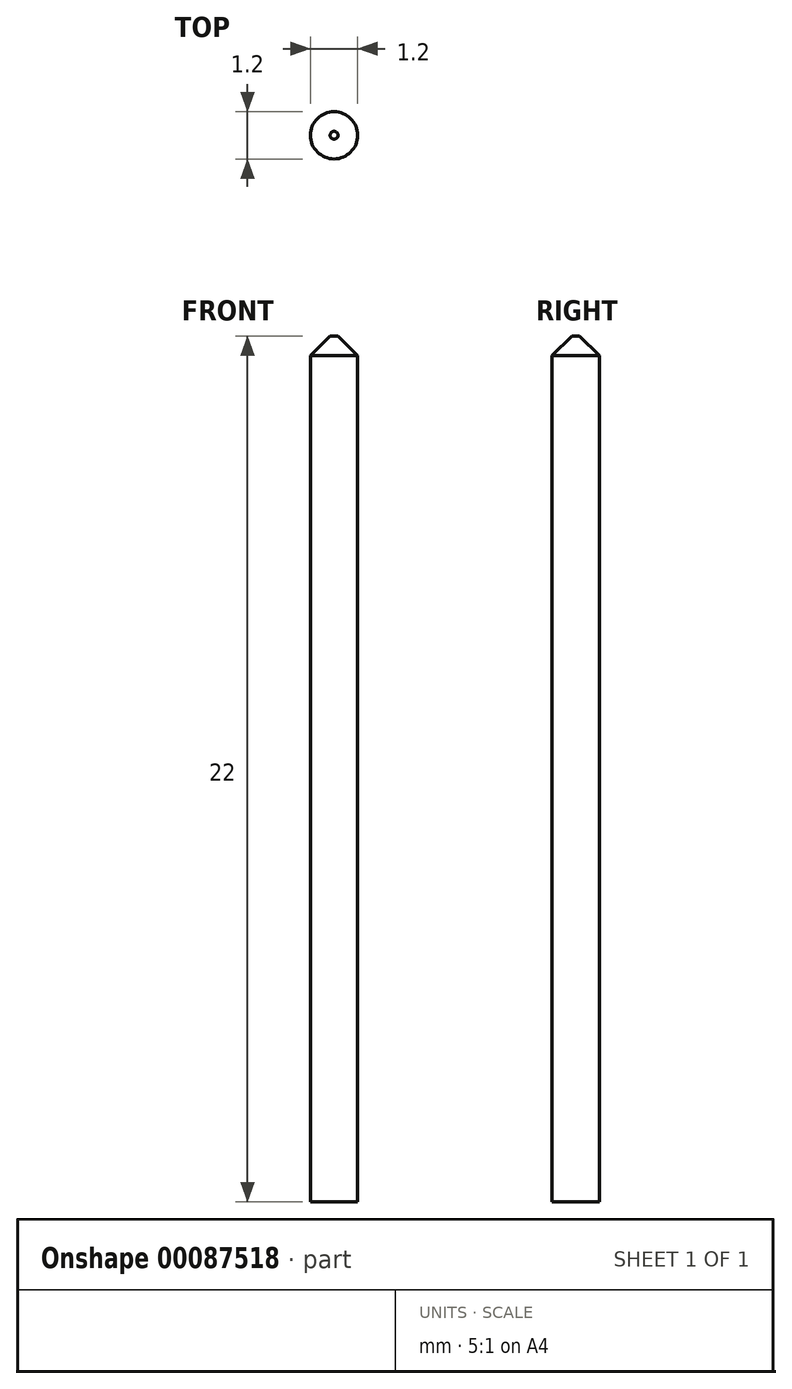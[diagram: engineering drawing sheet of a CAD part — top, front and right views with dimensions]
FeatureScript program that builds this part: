
annotation { "Feature Type Name" : "Feature", "Feature Type Description" : "" }
export const myFeature = defineFeature(function(context is Context, id is Id, definition is map)
    precondition{}
    {
        {
            var Q0;
            Q0=qCreatedBy(makeId("Top.planeOp"),FACE);
            var sketch = newSketch(context, id + "F0", { "sketchPlane" : qUnion([Q0])});
            skCircle(sketch, "E0", {"center": v(0, 0) * mm, "radius": 0.6 * mm});
            skSolve(sketch);
        }
        {
            var Q0;
            Q0 = qSketchRegion(id + "F0", true);
            extrude(context, id + "F1", {"entities" : qUnion([Q0]), "depth" : 22 * mm});
        }
        {
            var Q0;
            Q0=makeQuery(id+"F1.opExtrude","CAP_EDGE",EDGE,{"disambiguationData":[OSD([sQuery(id+"F0.wireOp",EDGE,"E0")])],"isStart":false});
            chamfer(context, id + "F2", {"entities" : qUnion([Q0]), "width" : .5 * mm, "tangentPropagation" : true});
        }
    });
